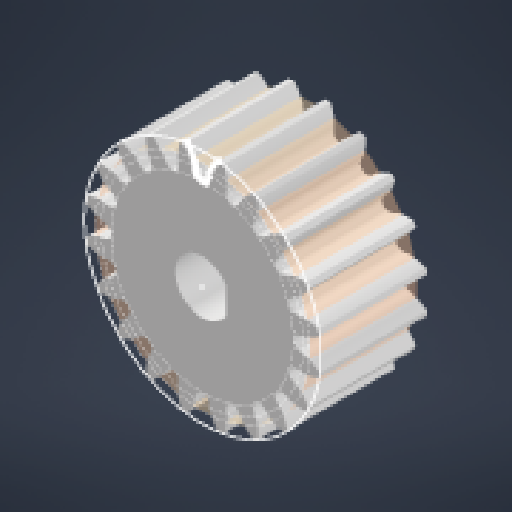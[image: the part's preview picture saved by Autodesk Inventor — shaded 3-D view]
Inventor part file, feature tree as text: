
AUTODESK INVENTOR PART (.ipt)
format: ipt  version: 2023.2 (Build 272271000, 271)  size: 350,208 bytes
history: native  units: mm
features: sketch x5, extrude x4, pattern_circular x1, hole x1, other x1
ambient origin geometry x8: Origin, YZ Plane, XZ Plane, XY Plane, X Axis, Y Axis, Z Axis, Center Point
bodies: Solid1 (feature_tree)
feature tree (12):
  sketch  "Sketch1"  dims[d0=10.0mm d1=0.0mm]
  extrude  "Extrusion1"  TaperAngle=0.0deg  [1 undecoded]
  extrude  "Extrusion2"  Depth=10.0mm TaperAngle=360.0deg
  pattern_circular  "Circular Pattern1"  [2 undecoded]
  hole  "Hole1"  [1 undecoded]
  sketch  "Sketch2"  dims[d2=10.0mm d3=0.0mm d4=200.0mm d5=360.0deg]
  sketch  "Sketch3"  dims[d7=5.0mm d8=6.0mm d9=4.0mm d10=2.0mm d11=90.0deg d12=8.0mm d13=20.594885mm]
  extrude  "Extrusion3"  [1 undecoded]
  sketch  "Sketch4"  dims[d14=10.0mm d15=0.0mm]
  sketch  "Sketch5"  dims[d16=0.0mm d17=0.0mm d18=0.375mm]
  other  "Srf1"
  extrude  "ExtrusionSrf1"  [1 undecoded]
note: 6 required parameter values undecoded (feature->parameter linkage not recoverable at this tier; creation-order binding heuristic only, values carry confidence <= 0.55)
